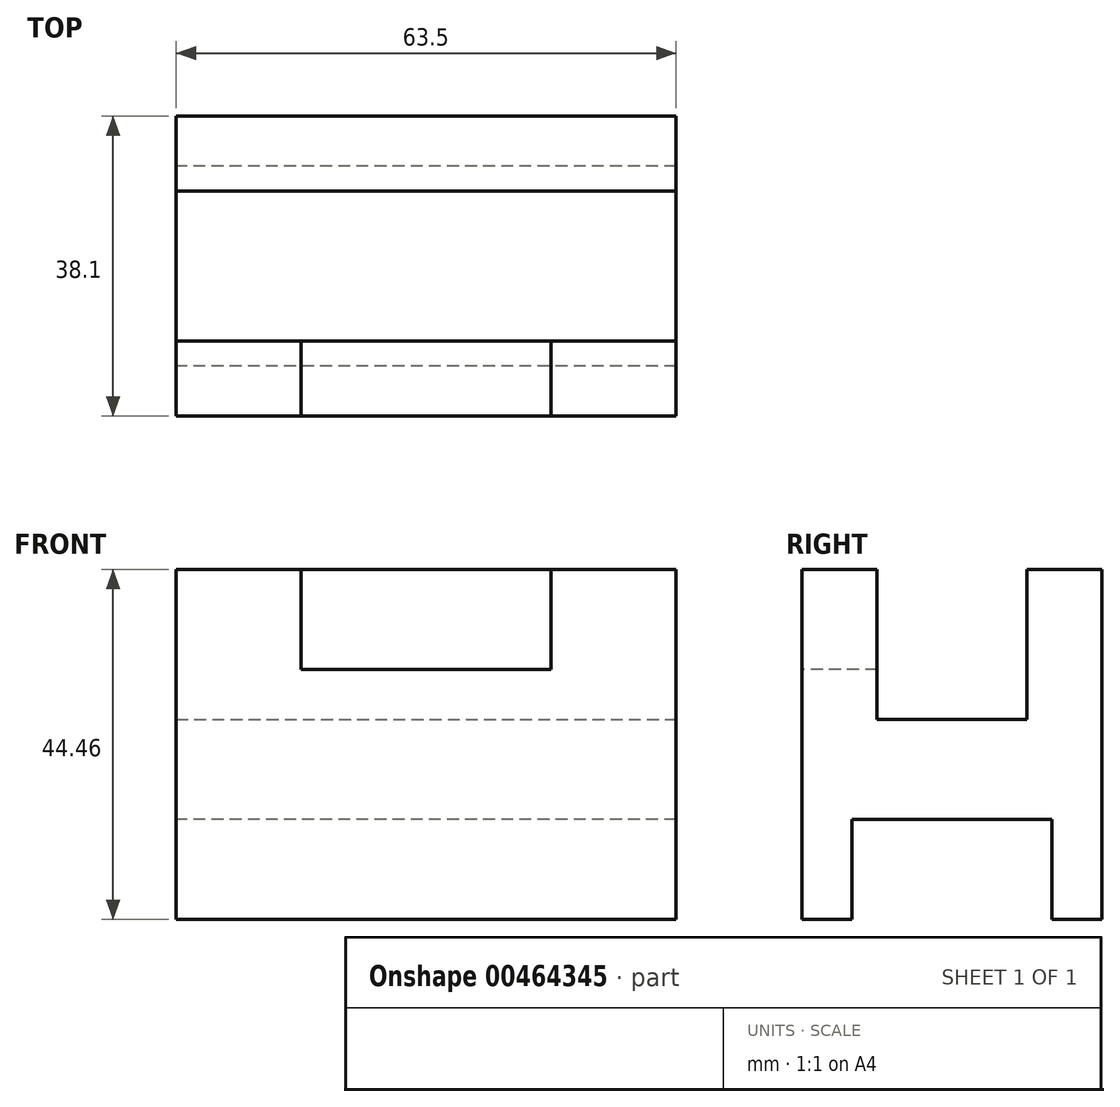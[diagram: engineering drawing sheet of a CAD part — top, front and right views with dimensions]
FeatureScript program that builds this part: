
annotation { "Feature Type Name" : "Feature", "Feature Type Description" : "" }
export const myFeature = defineFeature(function(context is Context, id is Id, definition is map)
    precondition{}
    {
        {
            var Q0;
            Q0=qCreatedBy(makeId("Front.planeOp"),FACE);
            var sketch = newSketch(context, id + "F0", { "sketchPlane" : qUnion([Q0])});
            skLineSegment(sketch, "E0.bottom", {"start": v(-31.75, 22.22) * mm, "end": v(31.75, 22.22) * mm});
            skLineSegment(sketch, "E0.top", {"start": v(-31.75, -22.22) * mm, "end": v(31.75, -22.22) * mm});
            skLineSegment(sketch, "E0.left", {"start": v(-31.75, 22.22) * mm, "end": v(-31.75, -22.22) * mm});
            skLineSegment(sketch, "E0.right", {"start": v(31.75, 22.22) * mm, "end": v(31.75, -22.22) * mm});
            skPoint(sketch, "E0.middle", {"position": v(0, 0) * mm});
            skLineSegment(sketch, "E1.bottom", {"start": v(15.87, 22.22) * mm, "end": v(-15.87, 22.22) * mm});
            skLineSegment(sketch, "E1.top", {"start": v(15.87, 9.53) * mm, "end": v(-15.87, 9.53) * mm});
            skLineSegment(sketch, "E1.left", {"start": v(15.87, 22.23) * mm, "end": v(15.87, 9.53) * mm});
            skLineSegment(sketch, "E1.right", {"start": v(-15.87, 22.23) * mm, "end": v(-15.87, 9.53) * mm});
            skSolve(sketch);
        }
        {
            var Q0;
            Q0=makeQuery(id+"F0.imprint","IMPRINT",FACE,{"disambiguationData":[TD([[makeQuery(id+"F0.imprint","IMPRINT",EDGE,{"derivedFrom":sQuery(id+"F0.wireOp",EDGE,"E0.top")}),1.0]])]});
            extrude(context, id + "F1", {"entities" : qUnion([Q0]), "depth" : 38.1 * mm});
        }
        {
            var Q0;
            Q0=makeQuery(id+"F1.opExtrude","SWEPT_FACE",FACE,{"disambiguationData":[OSD([sQuery(id+"F0.wireOp",EDGE,"E1.left")])]});
            extrude(context, id + "F2", {"entities" : qUnion([Q0]), "operationType" : NewBodyOperationType.ADD, "depth" : 31.75 * mm});
        }
        {
            var Q0;
            {var subQ0=sQuery(id+"F0.wireOp",EDGE,"E1.left");Q0=makeQuery(id+"F2.boolean.opBoolean","MERGE",FACE,{"derivedFrom":[makeQuery(id+"F1.opExtrude","CAP_FACE",FACE,{"disambiguationData":[OSD([sQuery(id+"F0.wireOp",EDGE,"E0.bottom"),sQuery(id+"F0.wireOp",EDGE,"E0.top"),sQuery(id+"F0.wireOp",EDGE,"E0.left"),sQuery(id+"F0.wireOp",EDGE,"E0.right"),sQuery(id+"F0.wireOp",EDGE,"E1.top"),subQ0,sQuery(id+"F0.wireOp",EDGE,"E1.right")])],"isStart":false}),makeQuery(id+"F2.opExtrude","SWEPT_FACE",FACE,{"disambiguationData":[OSD([subQ0]),TDD([makeQuery(id+"F1.opExtrude","CAP_EDGE",EDGE,{"disambiguationData":[OSD([subQ0])],"isStart":false})])]})]});}
            var sketch = newSketch(context, id + "F3", { "sketchPlane" : qUnion([Q0])});
            skLineSegment(sketch, "E2.bottom", {"start": v(15.88, 22.22) * mm, "end": v(-15.87, 22.22) * mm});
            skLineSegment(sketch, "E2.top", {"start": v(15.88, 9.53) * mm, "end": v(-15.87, 9.53) * mm});
            skLineSegment(sketch, "E2.left", {"start": v(15.88, 22.22) * mm, "end": v(15.88, 9.53) * mm});
            skLineSegment(sketch, "E2.right", {"start": v(-15.87, 22.22) * mm, "end": v(-15.87, 9.53) * mm});
            skSolve(sketch);
        }
        {
            var Q0;
            Q0=makeQuery(id+"F3.imprint","IMPRINT",FACE,{"disambiguationData":[TD([[makeQuery(id+"F3.imprint","IMPRINT",EDGE,{"derivedFrom":sQuery(id+"F3.wireOp",EDGE,"E2.bottom")}),-1.0]])]});
            extrude(context, id + "F4", {"entities" : qUnion([Q0]), "operationType" : NewBodyOperationType.REMOVE, "oppositeDirection" : true, "depth" : 28.57 * mm});
        }
        {
            var Q0;
            Q0=makeQuery(id+"F1.opExtrude","SWEPT_FACE",FACE,{"disambiguationData":[OSD([sQuery(id+"F0.wireOp",EDGE,"E0.right")])]});
            var sketch = newSketch(context, id + "F5", { "sketchPlane" : qUnion([Q0])});
            skLineSegment(sketch, "E3.bottom", {"start": v(-9.53, 22.23) * mm, "end": v(-28.58, 22.23) * mm});
            skLineSegment(sketch, "E3.top", {"start": v(-9.52, 3.18) * mm, "end": v(-28.57, 3.18) * mm});
            skLineSegment(sketch, "E3.left", {"start": v(-9.53, 22.23) * mm, "end": v(-9.52, 3.18) * mm});
            skLineSegment(sketch, "E3.right", {"start": v(-28.58, 22.23) * mm, "end": v(-28.57, 3.18) * mm});
            skSolve(sketch);
        }
        {
            var Q0;
            Q0=makeQuery(id+"F5.imprint","IMPRINT",FACE,{"disambiguationData":[TD([[makeQuery(id+"F5.imprint","IMPRINT",EDGE,{"derivedFrom":sQuery(id+"F5.wireOp",EDGE,"E3.bottom")}),-1.0]])]});
            extrude(context, id + "F6", {"entities" : qUnion([Q0]), "operationType" : NewBodyOperationType.REMOVE, "endBound" : BoundingType.THROUGH_ALL, "oppositeDirection" : true, "depth" : 63.5 * mm});
        }
        {
            var Q0;
            Q0=makeQuery(id+"F1.opExtrude","SWEPT_FACE",FACE,{"disambiguationData":[OSD([sQuery(id+"F0.wireOp",EDGE,"E0.left")])]});
            var sketch = newSketch(context, id + "F7", { "sketchPlane" : qUnion([Q0])});
            skLineSegment(sketch, "E4.bottom", {"start": v(31.75, -22.23) * mm, "end": v(6.35, -22.23) * mm});
            skLineSegment(sketch, "E4.top", {"start": v(31.75, -9.52) * mm, "end": v(6.35, -9.52) * mm});
            skLineSegment(sketch, "E4.left", {"start": v(31.75, -22.23) * mm, "end": v(31.75, -9.52) * mm});
            skLineSegment(sketch, "E4.right", {"start": v(6.35, -22.23) * mm, "end": v(6.35, -9.52) * mm});
            skSolve(sketch);
        }
        {
            var Q0;
            Q0=makeQuery(id+"F7.imprint","IMPRINT",FACE,{"disambiguationData":[TD([[makeQuery(id+"F7.imprint","IMPRINT",EDGE,{"derivedFrom":sQuery(id+"F7.wireOp",EDGE,"E4.bottom")}),-1.0]])]});
            extrude(context, id + "F8", {"entities" : qUnion([Q0]), "operationType" : NewBodyOperationType.REMOVE, "oppositeDirection" : true, "depth" : 63.5 * mm});
        }
    });
